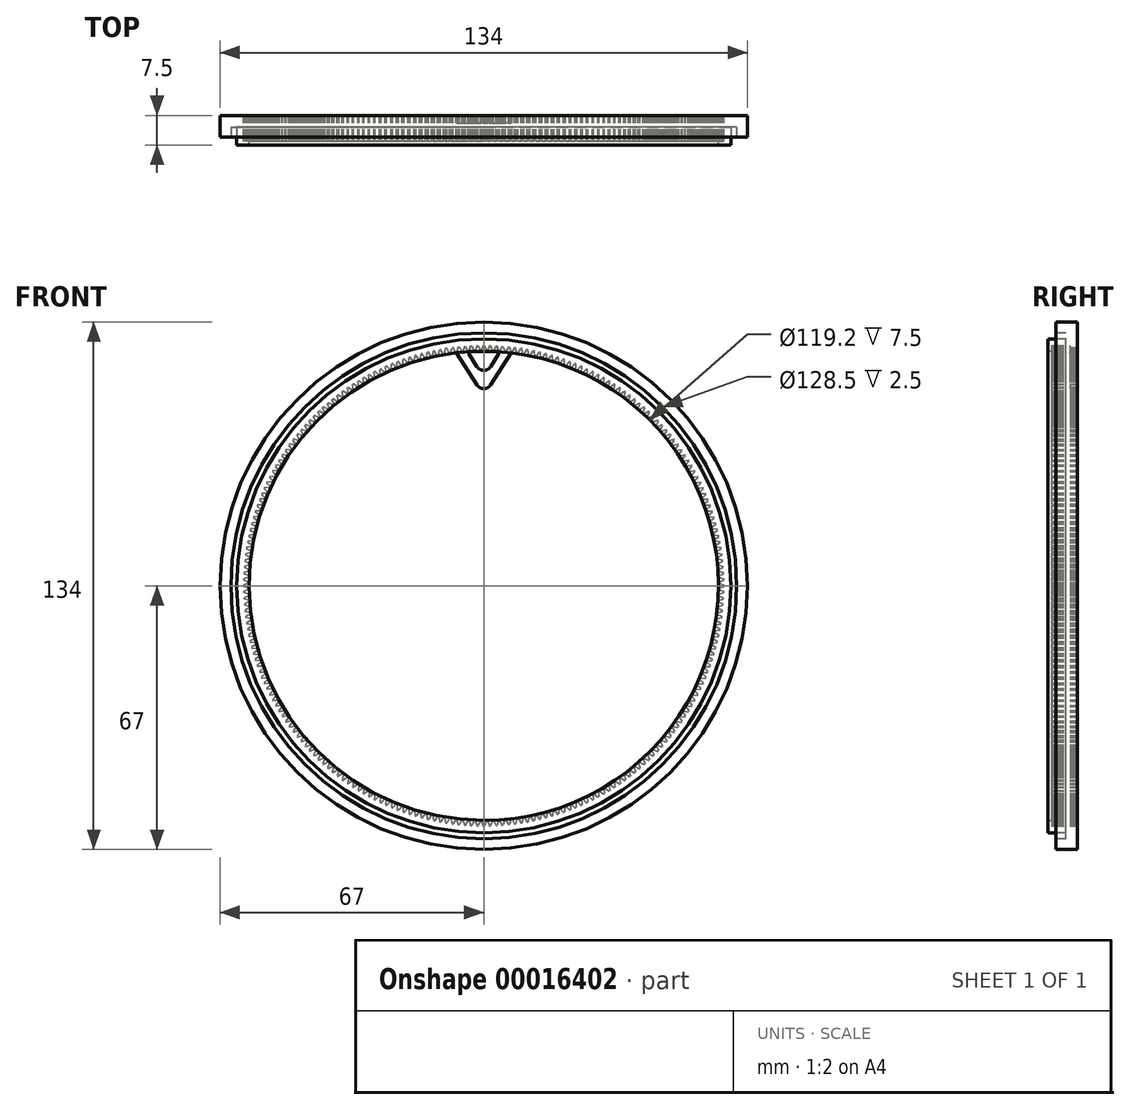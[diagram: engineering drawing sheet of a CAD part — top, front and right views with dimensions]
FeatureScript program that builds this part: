
annotation { "Feature Type Name" : "Feature", "Feature Type Description" : "" }
export const myFeature = defineFeature(function(context is Context, id is Id, definition is map)
    precondition{}
    {
        {
            var Q0;
            Q0=qCreatedBy(makeId("Front.planeOp"),FACE);
            var sketch = newSketch(context, id + "F0", { "sketchPlane" : qUnion([Q0])});
            skCircle(sketch, "E0", {"center": v(0, 0) * mm, "radius": 67 * mm});
            skCircle(sketch, "E1", {"center": v(0, 0) * mm, "radius": 59.6 * mm});
            skSolve(sketch);
        }
        {
            var Q0;
            Q0 = qSketchRegion(id + "F0", true);
            extrude(context, id + "F1", {"entities" : qUnion([Q0]), "endBound" : BoundingType.SYMMETRIC, "depth" : 7.5 * mm});
        }
        {
            var Q0;
            Q0=makeQuery(id+"F1.opExtrude","CAP_FACE",FACE,{"disambiguationData":[OSD([sQuery(id+"F0.wireOp",EDGE,"E0"),sQuery(id+"F0.wireOp",EDGE,"E1")])],"isStart":false});
            var sketch = newSketch(context, id + "F2", { "sketchPlane" : qUnion([Q0])});
            skCircle(sketch, "E2", {"center": v(0, 0) * mm, "radius": 63.5 * mm, "construction": true});
            skCircle(sketch, "E3", {"center": v(0, 0) * mm, "radius": 62.75 * mm});
            skCircle(sketch, "E4", {"center": v(0, 0) * mm, "radius": 64.25 * mm});
            skLineSegment(sketch, "E5", {"start": v(0, 62.75) * mm, "end": v(0, 63.5) * mm, "construction": true});
            skLineSegment(sketch, "E6", {"start": v(0, 63.5) * mm, "end": v(0, 64.25) * mm, "construction": true});
            skSolve(sketch);
        }
        {
            var Q0;
            Q0 = qSketchRegion(id + "F2", true);
            extrude(context, id + "F3", {"entities" : qUnion([Q0]), "operationType" : NewBodyOperationType.REMOVE, "oppositeDirection" : true, "depth" : 4.5 * mm});
        }
        {
            var Q0;
            Q0=makeQuery(id+"F2.imprint","IMPRINT",FACE,{"disambiguationData":[TD([[makeQuery(id+"F2.imprint","IMPRINT",EDGE,{"derivedFrom":sQuery(id+"F2.wireOp",EDGE,"E4")}),-1.0]])]});
            extrude(context, id + "F4", {"entities" : qUnion([Q0]), "operationType" : NewBodyOperationType.REMOVE, "oppositeDirection" : true, "depth" : 2 * mm});
        }
        {
            var Q0;
            Q0=makeQuery(id+"F1.opExtrude","CAP_FACE",FACE,{"disambiguationData":[OSD([sQuery(id+"F0.wireOp",EDGE,"E0"),sQuery(id+"F0.wireOp",EDGE,"E1")])],"isStart":true});
            var sketch = newSketch(context, id + "F5", { "sketchPlane" : qUnion([Q0])});
            skCircle(sketch, "E7", {"center": v(0, 0) * mm, "radius": 61 * mm, "construction": true});
            skLineSegment(sketch, "E8", {"start": v(59.6, 0.68) * mm, "end": v(59.6, -0.68) * mm});
            skLineSegment(sketch, "E9", {"start": v(0, 0) * mm, "end": v(59.6, 0) * mm, "construction": true});
            skLineSegment(sketch, "E10", {"start": v(61, 0.15) * mm, "end": v(61, -0.15) * mm});
            skLineSegment(sketch, "E11", {"start": v(59.6, 0) * mm, "end": v(61, 0) * mm, "construction": true});
            skLineSegment(sketch, "E12", {"start": v(59.6, 0.68) * mm, "end": v(61, 0.15) * mm});
            skLineSegment(sketch, "E13", {"start": v(59.6, -0.68) * mm, "end": v(61, -0.15) * mm});
            skSolve(sketch);
        }
        {
            var Q0;
            Q0 = qSketchRegion(id + "F5", true);
            extrude(context, id + "F6", {"entities" : qUnion([Q0]), "operationType" : NewBodyOperationType.REMOVE, "oppositeDirection" : true, "depth" : 6.5 * mm});
        }
        {
            var Q0;
            Q0=makeQuery(id+"F6.boolean.opBoolean","COPY",FACE,{"derivedFrom":makeQuery(id+"F6.opExtrude","SWEPT_FACE",FACE,{"disambiguationData":[OSD([sQuery(id+"F5.wireOp",EDGE,"E12")])]})});
            var Q1;
            Q1=makeQuery(id+"F6.boolean.opBoolean","COPY",FACE,{"derivedFrom":makeQuery(id+"F6.opExtrude","SWEPT_FACE",FACE,{"disambiguationData":[OSD([sQuery(id+"F5.wireOp",EDGE,"E10")])]})});
            var Q2;
            Q2=makeQuery(id+"F6.boolean.opBoolean","COPY",FACE,{"derivedFrom":makeQuery(id+"F6.opExtrude","SWEPT_FACE",FACE,{"disambiguationData":[OSD([sQuery(id+"F5.wireOp",EDGE,"E13")])]})});
            var Q3;
            Q3=makeQuery(id+"F6.boolean.opBoolean","COPY",FACE,{"derivedFrom":makeQuery(id+"F6.opExtrude","CAP_FACE",FACE,{"disambiguationData":[OSD([sQuery(id+"F5.wireOp",EDGE,"E8"),sQuery(id+"F5.wireOp",EDGE,"E10"),sQuery(id+"F5.wireOp",EDGE,"E12"),sQuery(id+"F5.wireOp",EDGE,"E13")])],"isStart":false})});
            var Q4;
            Q4=makeQuery(id+"F1.opExtrude","CAP_EDGE",EDGE,{"disambiguationData":[OSD([sQuery(id+"F0.wireOp",EDGE,"E1")])],"isStart":false});
            circularPattern(context, id + "F7", {"faces" : qUnion([Q0, Q1, Q2, Q3]), "axis" : qUnion([Q4]), "angle" : 360 * degree, "instanceCount" : 240, "equalSpace" : true, "patternType" : PatternType.FACE});
        }
        {
            var Q0;
            Q0=makeQuery(id+"F1.opExtrude","CAP_FACE",FACE,{"disambiguationData":[OSD([sQuery(id+"F0.wireOp",EDGE,"E0"),sQuery(id+"F0.wireOp",EDGE,"E1")])],"isStart":true});
            var sketch = newSketch(context, id + "F8", { "sketchPlane" : qUnion([Q0])});
            skLineSegment(sketch, "E14", {"start": v(-8.71, 61.98) * mm, "end": v(8.71, 61.98) * mm});
            skLineSegment(sketch, "E15", {"start": v(8.71, 61.98) * mm, "end": v(0, 48.36) * mm});
            skLineSegment(sketch, "E16", {"start": v(0, 48.36) * mm, "end": v(-8.71, 61.98) * mm});
            skLineSegment(sketch, "E17", {"start": v(8.71, 61.98) * mm, "end": v(0, 0) * mm, "construction": true});
            skLineSegment(sketch, "E18.0", {"start": v(-4.15, 59.48) * mm, "end": v(4.15, 59.48) * mm});
            skLineSegment(sketch, "E18.1", {"start": v(0, 53) * mm, "end": v(-4.15, 59.48) * mm});
            skLineSegment(sketch, "E18.2", {"start": v(4.15, 59.48) * mm, "end": v(0, 53) * mm});
            skLineSegment(sketch, "E19", {"start": v(0, 53) * mm, "end": v(0, 0) * mm, "construction": true});
            skSolve(sketch);
        }
        {
            var Q0;
            Q0 = qSketchRegion(id + "F8", true);
            extrude(context, id + "F9", {"entities" : qUnion([Q0]), "operationType" : NewBodyOperationType.ADD, "oppositeDirection" : true, "depth" : 2 * mm});
        }
        {
            var Q0;
            Q0=makeQuery(id+"F9.opExtrude","SWEPT_EDGE",EDGE,{"disambiguationData":[OSD([sQuery(id+"F8.wireOp",EDGE,"E15"),sQuery(id+"F8.wireOp",EDGE,"E16")])]});
            var Q1;
            Q1=makeQuery(id+"F9.opExtrude","SWEPT_EDGE",EDGE,{"disambiguationData":[OSD([sQuery(id+"F8.wireOp",EDGE,"E18.0"),sQuery(id+"F8.wireOp",EDGE,"E18.1")])]});
            var Q2;
            Q2=makeQuery(id+"F9.opExtrude","SWEPT_EDGE",EDGE,{"disambiguationData":[OSD([sQuery(id+"F8.wireOp",EDGE,"E18.1"),sQuery(id+"F8.wireOp",EDGE,"E18.2")])]});
            var Q3;
            Q3=makeQuery(id+"F9.opExtrude","SWEPT_EDGE",EDGE,{"disambiguationData":[OSD([sQuery(id+"F8.wireOp",EDGE,"E18.0"),sQuery(id+"F8.wireOp",EDGE,"E18.2")])]});
            fillet(context, id + "F10", {"entities" : qUnion([Q0, Q1, Q2, Q3]), "radius" : 2 * mm, "tangentPropagation" : true, "allowEdgeOverflow" : false});
        }
    });
